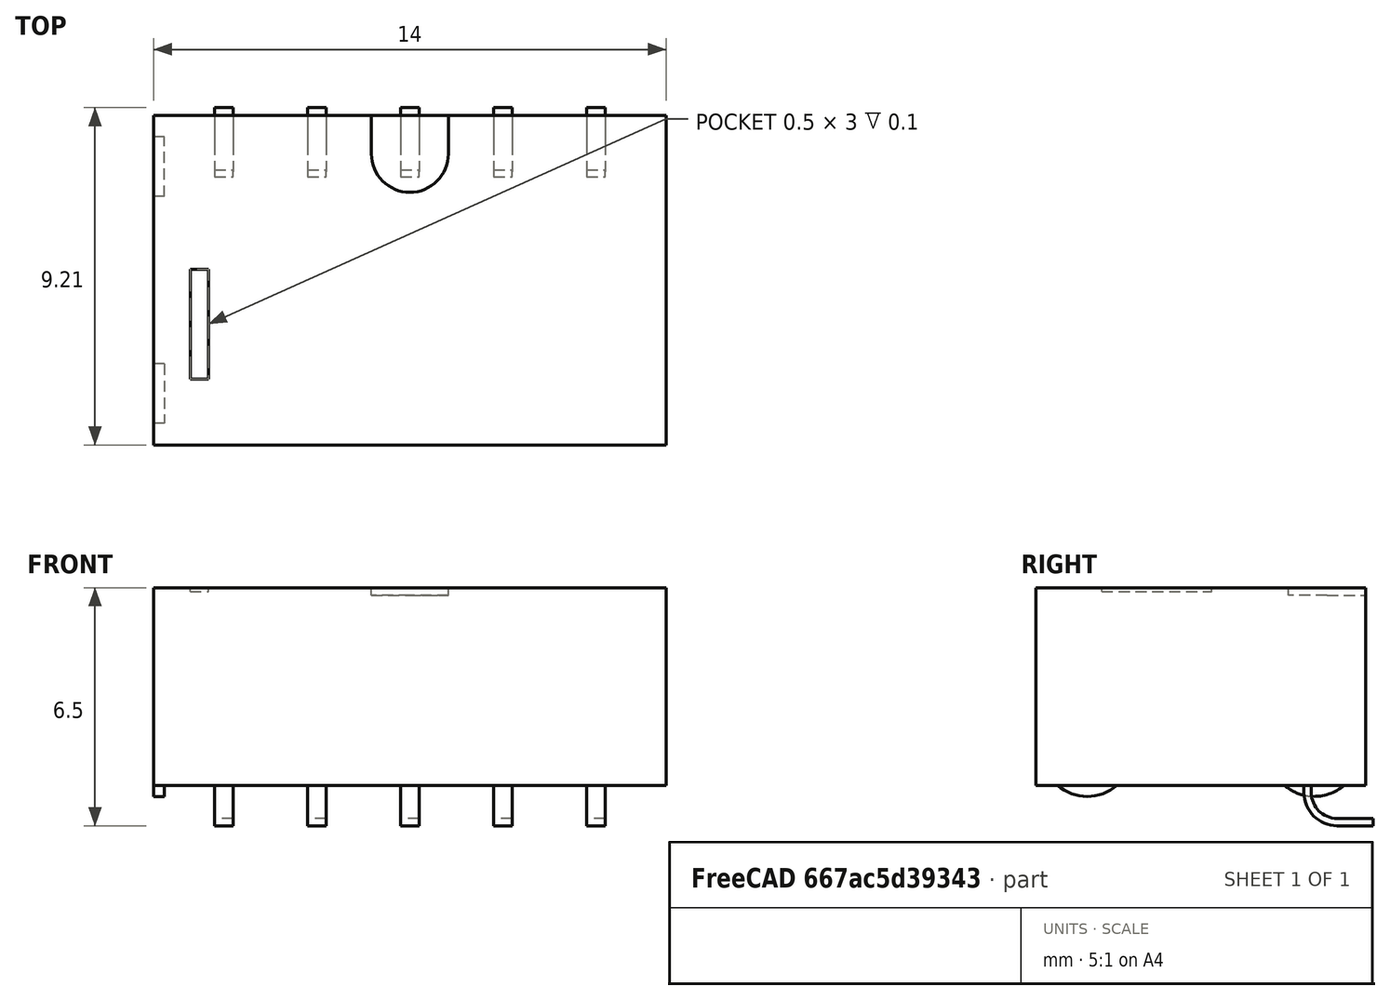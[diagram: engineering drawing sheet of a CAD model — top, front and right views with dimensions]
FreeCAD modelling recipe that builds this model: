
FCSTD DOCUMENT  (FreeCAD 0.18.4R)
Label: hfd31_5-l1s
License: All rights reserved
LicenseURL: http://en.wikipedia.org/wiki/All_rights_reserved
objects: Part::Mirroring×8, Part::Box×5, Part::Sweep×5, Part::Cut×3, Part::Cylinder×2, Part::MultiFuse×1
note: 24 computed .brp shape members not serialized (recipe doc carries the construction recipe); baked Part::Feature solids carry a one-line shape summary decoded from their .brp

FEATURE [Part::Box] Box  label="BodyMain"
  AttacherType = Attacher::AttachEngine3D
  Height = 5.4
  Length = 14
  Placement = pos=(-7,-4.5,1.1) rot=(0,0,1;0rad)
  Width = 9
  expr: Placement.Base.z = 6.5 - 5.4
  expr: Placement.Base.y = -(Width / 2)
  expr: Placement.Base.x = -(Length / 2)
FEATURE [Part::Box] Box001  label="BodyStripe"
  AttacherType = Attacher::AttachEngine3D
  Height = 0.1
  Length = 0.5
  Placement = pos=(-6,-2.7,6.4) rot=(0,0,1;0rad)
  Width = 3
FEATURE [Part::Box] Box002  label="BodyStripe001"
  AttacherType = Attacher::AttachEngine3D
  Height = 0.1
  Length = 0.5
  Placement = pos=(-6,-2.7,6.4) rot=(0,0,1;0rad)
  Width = 3
FEATURE [Part::Cut] Cut
  Base = -> Box
  Tool = -> Box002
FEATURE [Part::Cylinder] Cylinder
  Angle = 360
  AttacherType = Attacher::AttachEngine3D
  Height = 0.2
  Placement = pos=(0,3.45,6.3) rot=(0,0,1;0rad)
  Radius = 1.05
  expr: Placement.Base.y = 4.5 - 1.05
FEATURE [Part::Box] Box003  label="Cube"
  AttacherType = Attacher::AttachEngine3D
  Height = 0.2
  Length = 2.1
  Placement = pos=(-1.05,3.45,6.3) rot=(0,0,1;0rad)
  Width = 1.05
FEATURE [Part::MultiFuse] Fusion
  Shapes = -> [Box003,Cylinder]
FEATURE [Part::Cut] Cut001
  Base = -> Cut
  Tool = -> Fusion
FEATURE [Part::Cylinder] Cylinder001
  Angle = 180
  AttacherType = Attacher::AttachEngine3D
  Height = 0.3
  Placement = pos=(6.7,3.1,2.05) rot=(0.57735,-0.57735,0.57735;4.18879rad)
  Radius = 1.25
  expr: Placement.Base.x = 7 - 0.3
FEATURE [Part::Box] Box004  label="Cube001"
  AttacherType = Attacher::AttachEngine3D
  Height = 2
  Length = 0.3
  Placement = pos=(6.7,1.5,1.1) rot=(0,0,1;0rad)
  Width = 3
FEATURE [Part::Cut] Cut002
  Base = -> Cylinder001
  Tool = -> Box004
FEATURE [Part::Mirroring] Part__Mirroring  label="Cut002 (Mirror #1)"
  Base = (0,0,0)
  Normal = (0,1,0)
  Source = -> Cut002
FEATURE [Part::Mirroring] Part__Mirroring001  label="Cut002 (Mirror #2)"
  Base = (0,0,0)
  Normal = (1,0,0)
  Source = -> Cut002
FEATURE [Part::Mirroring] Part__Mirroring002  label="Cut002 (Mirror #3)"
  Base = (0,0,0)
  Normal = (1,0,0)
  Source = -> Part__Mirroring
FEATURE [Part::Sweep] Sweep
  Frenet = false
  Placement = pos=(0,-4.71,0.1) rot=(0,0,1;0rad)
  Solid = true
  Transition = 1
  expr: Placement.Base.y = -(11.2 / 2 - 0.89)
FEATURE [Part::Sweep] Sweep001
  Frenet = false
  Placement = pos=(2.54,-4.71,0.1) rot=(0,0,1;0rad)
  Solid = true
  Transition = 1
  expr: Placement.Base.y = -(11.2 / 2 - 0.89)
FEATURE [Part::Sweep] Sweep002
  Frenet = false
  Placement = pos=(5.08,-4.71,0.1) rot=(0,0,1;0rad)
  Solid = true
  Transition = 1
  expr: Placement.Base.y = -(11.2 / 2 - 0.89)
FEATURE [Part::Sweep] Sweep003
  Frenet = false
  Placement = pos=(-2.54,-4.71,0.1) rot=(0,0,1;0rad)
  Solid = true
  Transition = 1
  expr: Placement.Base.y = -(11.2 / 2 - 0.89)
FEATURE [Part::Sweep] Sweep004
  Frenet = false
  Placement = pos=(-5.08,-4.71,0.1) rot=(0,0,1;0rad)
  Solid = true
  Transition = 1
  expr: Placement.Base.y = -(11.2 / 2 - 0.89)
FEATURE [Part::Mirroring] Part__Mirroring003  label="Sweep (Mirror #4)"
  Base = (0,0,0)
  Normal = (0,1,0)
  Source = -> Sweep
FEATURE [Part::Mirroring] Part__Mirroring004  label="Sweep001 (Mirror #5)"
  Base = (0,0,0)
  Normal = (0,1,0)
  Source = -> Sweep001
FEATURE [Part::Mirroring] Part__Mirroring005  label="Sweep002 (Mirror #6)"
  Base = (0,0,0)
  Normal = (0,1,0)
  Source = -> Sweep002
FEATURE [Part::Mirroring] Part__Mirroring006  label="Sweep003 (Mirror #7)"
  Base = (0,0,0)
  Normal = (0,1,0)
  Source = -> Sweep003
FEATURE [Part::Mirroring] Part__Mirroring007  label="Sweep004 (Mirror #8)"
  Base = (0,0,0)
  Normal = (0,1,0)
  Source = -> Sweep004
